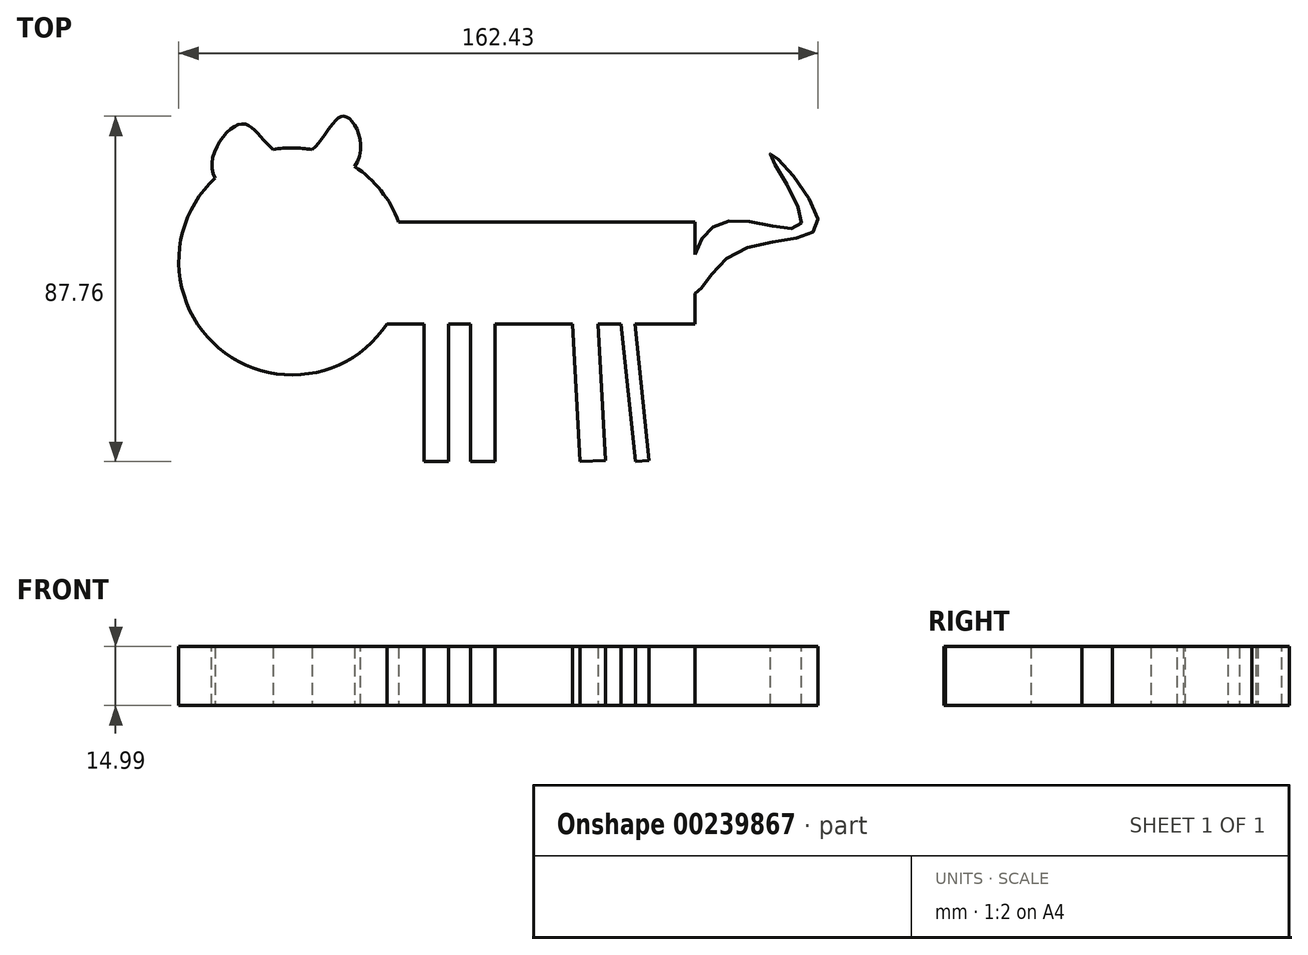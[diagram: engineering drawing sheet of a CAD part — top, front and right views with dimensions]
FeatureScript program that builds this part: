
annotation { "Feature Type Name" : "Feature", "Feature Type Description" : "" }
export const myFeature = defineFeature(function(context is Context, id is Id, definition is map)
    precondition{}
    {
        {
            var Q0;
            Q0=qCreatedBy(makeId("Top.planeOp"),FACE);
            var sketch = newSketch(context, id + "F0", { "sketchPlane" : qUnion([Q0])});
            skArc(sketch, "E0", {"start": v(-27.51, 33.16) * mm, "mid": v(-32, 41.13) * mm, "end": v(-38.75, 47.29) * mm});
            skLineSegment(sketch, "E1", {"start": v(-30.48, 7.32) * mm, "end": v(-21.1, 7.32) * mm});
            skLineSegment(sketch, "E2", {"start": v(-27.51, 33.16) * mm, "end": v(47.8, 33.16) * mm});
            skLineSegment(sketch, "E3", {"start": v(47.8, 7.32) * mm, "end": v(47.8, 15.05) * mm});
            skFitSpline(sketch, "E4", {"points": [v(47.8, 24.89) * mm, v(57.93, 33.6) * mm, v(74.8, 33.04) * mm, v(66.93, 50.48) * mm, v(79.03, 33.04) * mm, v(58.21, 25.45) * mm, v(47.8, 15.05) * mm, v(47.8, 24.89) * mm]});
            skLineSegment(sketch, "E5.trimOffspring", {"start": v(47.8, 24.89) * mm, "end": v(47.8, 33.16) * mm});
            skFitSpline(sketch, "E6", {"points": [v(-74.12, 44.37) * mm, v(-67.78, 58.07) * mm, v(-59.38, 51.6) * mm, v(-49.5, 51.57) * mm, v(-41.34, 60.04) * mm, v(-38.75, 47.29) * mm, v(-74.12, 44.37) * mm]});
            skArc(sketch, "E7.trimOffspring", {"start": v(-74.12, 44.37) * mm, "mid": v(-73.23, 1.2) * mm, "end": v(-30.48, 7.32) * mm});
            skArc(sketch, "E8.trimOffspring", {"start": v(-49.5, 51.57) * mm, "mid": v(-54.44, 52.01) * mm, "end": v(-59.38, 51.6) * mm});
            skLineSegment(sketch, "E9", {"start": v(-21.1, 7.32) * mm, "end": v(-21.1, -27.7) * mm});
            skLineSegment(sketch, "E10", {"start": v(-21.1, -27.7) * mm, "end": v(-14.9, -27.7) * mm});
            skLineSegment(sketch, "E11", {"start": v(-14.9, -27.7) * mm, "end": v(-14.9, 7.32) * mm});
            skLineSegment(sketch, "E12", {"start": v(-9.28, 7.32) * mm, "end": v(-9.28, -27.7) * mm});
            skLineSegment(sketch, "E13", {"start": v(-9.28, -27.7) * mm, "end": v(-3.1, -27.7) * mm});
            skLineSegment(sketch, "E14", {"start": v(-3.1, -27.7) * mm, "end": v(-3.1, 7.32) * mm});
            skLineSegment(sketch, "E15", {"start": v(-3.1, 7.32) * mm, "end": v(16.6, 7.32) * mm});
            skLineSegment(sketch, "E16", {"start": v(16.6, 7.32) * mm, "end": v(18.56, -27.7) * mm});
            skLineSegment(sketch, "E17", {"start": v(18.56, -27.7) * mm, "end": v(25.07, -27.34) * mm});
            skLineSegment(sketch, "E18", {"start": v(25.07, -27.34) * mm, "end": v(23.12, 7.32) * mm});
            skLineSegment(sketch, "E19", {"start": v(23.12, 7.32) * mm, "end": v(28.97, 7.32) * mm});
            skLineSegment(sketch, "E20", {"start": v(28.97, 7.32) * mm, "end": v(32.62, -27.7) * mm});
            skLineSegment(sketch, "E21", {"start": v(32.62, -27.7) * mm, "end": v(36.13, -27.34) * mm});
            skLineSegment(sketch, "E22", {"start": v(36.13, -27.34) * mm, "end": v(32.51, 7.32) * mm});
            skLineSegment(sketch, "E23.trimOffspring", {"start": v(-14.9, 7.32) * mm, "end": v(-9.28, 7.32) * mm});
            skLineSegment(sketch, "E24.trimOffspring", {"start": v(32.51, 7.32) * mm, "end": v(47.8, 7.32) * mm});
            skSolve(sketch);
        }
        {
            var Q0;
            Q0 = qSketchRegion(id + "F0", true);
            extrude(context, id + "F1", {"entities" : qUnion([Q0]), "depth" : 15 * mm});
        }
    });
